# Revit family: R-MVD-0042
name_source: partatom
category: Portes
units: mm (PartAtom-declared; Revit-internal decimal feet)

## family parameters
Couper avec des vides une fois chargée = Non
Hôte = Mur
Partagée = Non
Point de calcul de pièce = Oui
Toujours verticalement = Oui

## types (1)
- MVD-0042
    ----- EQUIPEMENTS ----------------------- = .
    ----- PARAMETRES DE L'HÔTE -------------------- = .
    ----- PARAMETRES DES VANTAUX -------------------- = .
    ----- PARAMETRES POSITION HUISSERIE -------------------- = .
    ----- PARAMETRES PROFIL HUISSERIE -------------------- = .
    ----- TYPE DE PARCLOSAGE -------------------- = .
    ----- TYPE DE VANTAIL -------------------- = .
    ------INUTILISES-------------------------- = .
    ----PARAMETRES INUTILISES------------------------- = .
    1 Vantail = Non
    2 Vantaux = Oui
    Certification = D.A.S. Mode 2 certifié NF
    Coloris Verre = Verre
    Construction analytique = <Aucun>
    DAS = Oui
    Description = Bloc-porte vitré D.A.S. 2 vantaux avec bandeau GROOM et battement feuilluré, simple action, EI60, D.A.S. certifié NF, avec cadre et parcloses bois, sur huisserie bois
    Désaffleurement_Vantail = 4 mm  [stored 0.0131234 ft]
    Epaisseur joint = 4 mm  [stored 0.0131234 ft]
    Epaisseurs_Vantaux = 65 mm  [stored 0.213255 ft]
    FDES Inies = https://www.base-inies.fr
    Fabricant = MALERBA
    Fiche_Produit = MVD-0042
    Fonction = Intérieur
    Hauteur axe ventouse = 70 mm  [stored 0.229659 ft]
    Hauteur joint APD = 1140 mm  [stored 3.74016 ft]
    Hauteur_Axe_Bequille = 1045 mm  [stored 3.42848 ft]
    Hauteur_Vantaux_Souhaitée = 2040 mm  [stored 6.69291 ft]
    Jeu_Côté_Articulation_Vantail = 2 mm  [stored 0.00656168 ft]
    Jeu_Côté_Fermeture_Vantail = 3 mm  [stored 0.00984252 ft]
    Jeu_Traverse_Basse_Vantail = 7 mm  [stored 0.0229659 ft]
    Jeu_Traverse_Haute_Vantail = 3 mm  [stored 0.00984252 ft]
    Largeur Feuillure Battement Articulation = 15 mm  [stored 0.0492126 ft]
    Largeur joint APD = 36 mm  [stored 0.11811 ft]
    Largeur parclose = 32 mm  [stored 0.104987 ft]
    Largeur parclose recouvrement = 12 mm  [stored 0.0393701 ft]
    Largeur_Axe_Bequille = 50 mm  [stored 0.164042 ft]
    Largeur_Feuillure_Battement_Semi_Fixe = 15 mm  [stored 0.0492126 ft]
    Largeur_Feuillure_Battement_Service = 15 mm  [stored 0.0492126 ft]
    Largeur_Feuillure_Profil = 15 mm  [stored 0.0492126 ft]
    Largeur_Vantail_Semi_Fixe_Souhaitée = 630 mm  [stored 2.06693 ft]
    Largeur_Vantail_Service_Souhaitée = 930 mm  [stored 3.05118 ft]
    Materiaux_Dominant = Bois
    Modèle = 43 - SA-HB
    Note d'identification = 2V EI60 DAS VITRE - BANDEAU GROOM - FEUILLURE
    Parclosage Double = Non
    Parclosage Simple Coté Opposé Paumelles = Non
    Parclosage Simple Coté Paumelles = Oui
    Parclosage à Recouvrement = Non
    Paumelle Décalage Largeur Axe = 1 mm  [stored 0.00328084 ft]
    Paumelle Décalage Profondeur Axe = 8 mm  [stored 0.0262467 ft]
    Paumelle Position Largeur Axe = 0 mm  [stored 0 ft]
    Paumelle Position Profondeur Axe = 8 mm  [stored 0.0262467 ft]
    Paumelle_1 = 250 mm  [stored 0.82021 ft]
    Paumelle_2 = 1020 mm  [stored 3.34646 ft]
    Paumelle_3 = 1750 mm  [stored 5.74147 ft]
    Paumelle_4 = 1900 mm  [stored 6.2336 ft]
    Paumelle_5 = 500 mm  [stored 1.64042 ft]
    Porte Maternelle = Non
    Profondeur Feuillure Battement Articulation = 16 mm  [stored 0.0524934 ft]
    Profondeur parclose = 19 mm  [stored 0.062336 ft]
    Profondeur parclose recouvrement = 7 mm  [stored 0.0229659 ft]
    Profondeur_Feuillure_Battement_Semi_Fixe = 53 mm  [stored 0.173885 ft]
    Profondeur_Feuillure_Battement_Service = 16 mm  [stored 0.0524934 ft]
    Profondeur_Feuillure_Profil = 55 mm  [stored 0.180446 ft]
    Reference_Commerciale = 2V GV SA60 BANDEAU
    Reprise_Doublage_1 = 30 mm  [stored 0.0984252 ft]
    Reprise_Doublage_2 = 30 mm  [stored 0.0984252 ft]
    Reprise_Doublage_Haut = 30 mm  [stored 0.0984252 ft]
    Resistance_Feu = E60/EI60
    Sens_Feu = Recto / Verso
    Thermique (W/m2.°K) = 0
    URL = https://www.malerba.fr
    Ventouse = Oui
    Ventouse Position Largeur Axe = 120 mm  [stored 0.393701 ft]
    Visibilité poignée = Non
    Vitrage Epaisseur = 27 mm  [stored 0.0885827 ft]
    X_Largeur_Feuillure_Battement_Service = 15 mm  [stored 0.0492126 ft]

note: [stored X ft] marks values corroborated as IEEE doubles in the binary element streams (Revit-internal decimal feet)

## geometry (parser evidence)
native form markers: Blend x24
no freeform markers — native parametric forms only
